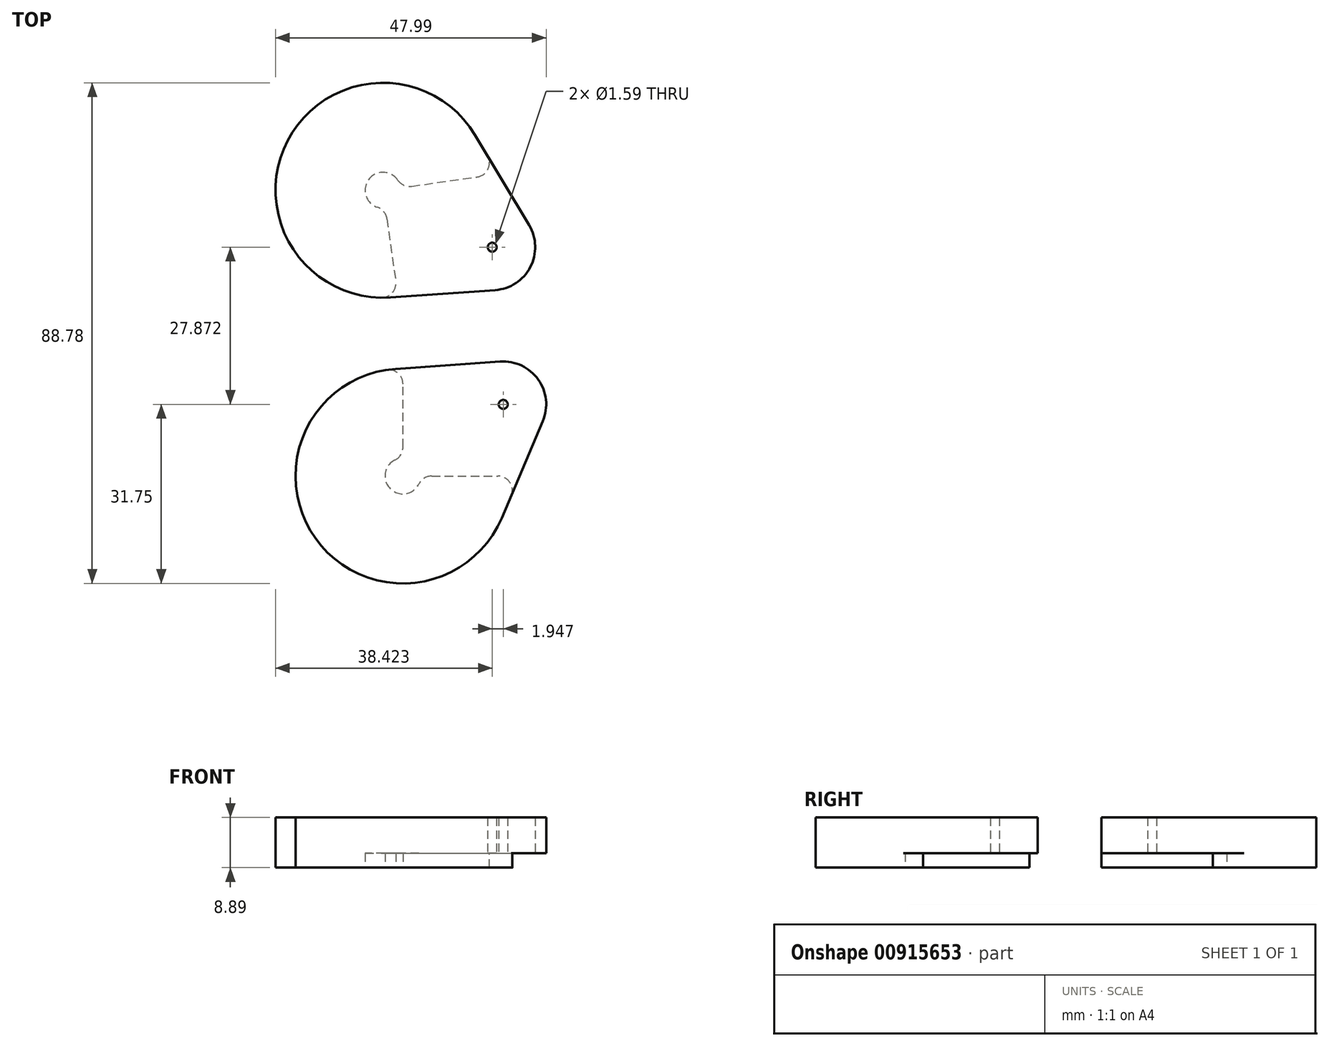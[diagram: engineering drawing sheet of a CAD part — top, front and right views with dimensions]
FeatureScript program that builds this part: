
annotation { "Feature Type Name" : "Feature", "Feature Type Description" : "" }
export const myFeature = defineFeature(function(context is Context, id is Id, definition is map)
    precondition{}
    {
        {
            var Q0;
            Q0=qCreatedBy(makeId("Top.planeOp"),FACE);
            var sketch = newSketch(context, id + "F0", { "sketchPlane" : qUnion([Q0])});
            skLineSegment(sketch, "E0.bottom", {"start": v(0, 0) * mm, "end": v(139.7, 0) * mm, "construction": true});
            skLineSegment(sketch, "E0.top", {"start": v(0, 1524) * mm, "end": v(139.7, 1524) * mm, "construction": true});
            skLineSegment(sketch, "E0.left", {"start": v(0, 0) * mm, "end": v(0, 1524) * mm, "construction": true});
            skLineSegment(sketch, "E0.right", {"start": v(139.7, 0) * mm, "end": v(139.7, 1524) * mm, "construction": true});
            skArc(sketch, "E1", {"start": v(-1.33, 19) * mm, "mid": v(-15.5, -11.07) * mm, "end": v(17.55, -7.42) * mm});
            skArc(sketch, "E2", {"start": v(24.8, 9.73) * mm, "mid": v(23.98, 17.13) * mm, "end": v(17.25, 20.3) * mm});
            skLineSegment(sketch, "E3", {"start": v(17.25, 20.3) * mm, "end": v(-1.33, 19) * mm});
            skLineSegment(sketch, "E4", {"start": v(24.8, 9.73) * mm, "end": v(17.55, -7.42) * mm});
            skSolve(sketch);
        }
        {
            var Q0;
            Q0 = qSketchRegion(id + "F0", true);
            extrude(context, id + "F1", {"entities" : qUnion([Q0]), "depth" : 8.9 * mm, "offsetDistance" : 25.4 * mm});
        }
        {
            var Q0;
            Q0=makeQuery(id+"F1.opExtrude","CAP_FACE",FACE,{"disambiguationData":[OSD([sQuery(id+"F0.wireOp",EDGE,"E1"),sQuery(id+"F0.wireOp",EDGE,"E2"),sQuery(id+"F0.wireOp",EDGE,"E3"),sQuery(id+"F0.wireOp",EDGE,"E4")])],"isStart":true});
            var sketch = newSketch(context, id + "F2", { "sketchPlane" : qUnion([Q0])});
            skLineSegment(sketch, "E5.bottom", {"start": v(0, 0) * mm, "end": v(52.3, 0) * mm});
            skLineSegment(sketch, "E5.top", {"start": v(0, -32.63) * mm, "end": v(52.3, -32.63) * mm});
            skLineSegment(sketch, "E5.left", {"start": v(0, 0) * mm, "end": v(0, -32.63) * mm});
            skLineSegment(sketch, "E5.right", {"start": v(52.3, 0) * mm, "end": v(52.3, -32.63) * mm});
            skSolve(sketch);
        }
        {
            var Q0;
            Q0 = qSketchRegion(id + "F2", true);
            extrude(context, id + "F3", {"entities" : qUnion([Q0]), "operationType" : NewBodyOperationType.REMOVE, "oppositeDirection" : true, "depth" : 2.54 * mm, "offsetDistance" : 25.4 * mm});
        }
        {
            var Q0;
            Q0=makeQuery(id+"F1.opExtrude","CAP_FACE",FACE,{"disambiguationData":[OSD([sQuery(id+"F0.wireOp",EDGE,"E1"),sQuery(id+"F0.wireOp",EDGE,"E2"),sQuery(id+"F0.wireOp",EDGE,"E3"),sQuery(id+"F0.wireOp",EDGE,"E4")])],"isStart":true});
            var sketch = newSketch(context, id + "F4", { "sketchPlane" : qUnion([Q0])});
            skCircle(sketch, "E6", {"center": v(0, 0) * mm, "radius": 3.17 * mm});
            skSolve(sketch);
        }
        {
            var Q0;
            Q0 = qSketchRegion(id + "F4", true);
            var Q1;
            Q1=makeQuery(id+"F3.boolean.opBoolean","COPY",FACE,{"derivedFrom":makeQuery(id+"F3.opExtrude","CAP_FACE",FACE,{"disambiguationData":[OSD([sQuery(id+"F2.wireOp",EDGE,"E5.bottom"),sQuery(id+"F2.wireOp",EDGE,"E5.top"),sQuery(id+"F2.wireOp",EDGE,"E5.left"),sQuery(id+"F2.wireOp",EDGE,"E5.right")])],"isStart":false})});
            extrude(context, id + "F5", {"entities" : qUnion([Q0]), "operationType" : NewBodyOperationType.REMOVE, "endBound" : BoundingType.UP_TO_SURFACE, "oppositeDirection" : true, "depth" : 25.4 * mm, "endBoundEntityFace" : qUnion([Q1]), "offsetDistance" : 25.4 * mm});
        }
        {
            var Q0;
            Q0=makeQuery(id+"F5.boolean.opBoolean","MERGE",FACE,{"derivedFrom":[makeQuery(id+"F3.boolean.opBoolean","COPY",FACE,{"derivedFrom":makeQuery(id+"F3.opExtrude","CAP_FACE",FACE,{"disambiguationData":[OSD([sQuery(id+"F2.wireOp",EDGE,"E5.bottom"),sQuery(id+"F2.wireOp",EDGE,"E5.top"),sQuery(id+"F2.wireOp",EDGE,"E5.left"),sQuery(id+"F2.wireOp",EDGE,"E5.right")])],"isStart":false})})],"fromTools":[makeQuery(id+"F5.opExtrude","CAP_FACE",FACE,{"disambiguationData":[OSD([sQuery(id+"F4.wireOp",EDGE,"E6")])],"isStart":false})]});
            var sketch = newSketch(context, id + "F6", { "sketchPlane" : qUnion([Q0])});
            skCircle(sketch, "E7", {"center": v(17.78, -12.7) * mm, "radius": 0.8 * mm});
            skSolve(sketch);
        }
        {
            var Q0;
            Q0 = qSketchRegion(id + "F6", true);
            extrude(context, id + "F7", {"entities" : qUnion([Q0]), "operationType" : NewBodyOperationType.REMOVE, "endBound" : BoundingType.THROUGH_ALL, "oppositeDirection" : true, "depth" : 25.4 * mm, "offsetDistance" : 25.4 * mm});
        }
        {
            var Q0;
            Q0=makeQuery(id+"F5.boolean.opBoolean","INTERSECT",EDGE,{"derivedFrom":[makeQuery(id+"F3.boolean.opBoolean","COPY",FACE,{"derivedFrom":makeQuery(id+"F3.opExtrude","SWEPT_FACE",FACE,{"disambiguationData":[OSD([sQuery(id+"F2.wireOp",EDGE,"E5.bottom")])]})}),makeQuery(id+"F5.opExtrude","SWEPT_FACE",FACE,{"disambiguationData":[OSD([sQuery(id+"F4.wireOp",EDGE,"E6")])]})]});
            var Q1;
            Q1=makeQuery(id+"F3.boolean.opBoolean","INTERSECT",EDGE,{"derivedFrom":[makeQuery(id+"F1.opExtrude","SWEPT_FACE",FACE,{"disambiguationData":[OSD([sQuery(id+"F0.wireOp",EDGE,"E4")])]}),makeQuery(id+"F3.opExtrude","SWEPT_FACE",FACE,{"disambiguationData":[OSD([sQuery(id+"F2.wireOp",EDGE,"E5.bottom")])]})]});
            var Q2;
            Q2=makeQuery(id+"F5.boolean.opBoolean","INTERSECT",EDGE,{"derivedFrom":[makeQuery(id+"F3.boolean.opBoolean","COPY",FACE,{"derivedFrom":makeQuery(id+"F3.opExtrude","SWEPT_FACE",FACE,{"disambiguationData":[OSD([sQuery(id+"F2.wireOp",EDGE,"E5.left")])]})}),makeQuery(id+"F5.opExtrude","SWEPT_FACE",FACE,{"disambiguationData":[OSD([sQuery(id+"F4.wireOp",EDGE,"E6")])]})]});
            var Q3;
            Q3=makeQuery(id+"F3.boolean.opBoolean","INTERSECT",EDGE,{"derivedFrom":[makeQuery(id+"F1.opExtrude","SWEPT_FACE",FACE,{"disambiguationData":[OSD([sQuery(id+"F0.wireOp",EDGE,"E3")])]}),makeQuery(id+"F3.opExtrude","SWEPT_FACE",FACE,{"disambiguationData":[OSD([sQuery(id+"F2.wireOp",EDGE,"E5.left")])]})]});
            fillet(context, id + "F8", {"entities" : qUnion([Q0, Q1, Q2, Q3]), "radius" : 2.54 * mm, "tangentPropagation" : true, "allowEdgeOverflow" : false});
        }
        {
            var Q0;
            Q0=makeQuery(id+"F1.opExtrude","SWEPT_FACE",FACE,{"disambiguationData":[OSD([sQuery(id+"F0.wireOp",EDGE,"E3")])]});
            cPlane(context, id + "F9", {"entities" : qUnion([Q0]), "cplaneType" : CPlaneType.OFFSET, "offset" : 6.35 * mm, "width" : 152.4 * mm, "height" : 152.4 * mm});
        }
        {
            var Q0;
            Q0=makeQuery(id+"F1.opExtrude","SWEPT_BODY",BODY,{"disambiguationData":[OSD([sQuery(id+"F0.wireOp",EDGE,"E1"),sQuery(id+"F0.wireOp",EDGE,"E2"),sQuery(id+"F0.wireOp",EDGE,"E3"),sQuery(id+"F0.wireOp",EDGE,"E4")])]});
            var Q1;
            Q1=qCreatedBy(id+"F9.planeOp",FACE);
            mirror(context, id + "F10", {"entities" : qUnion([Q0]), "mirrorPlane" : qUnion([Q1])});
        }
    });
